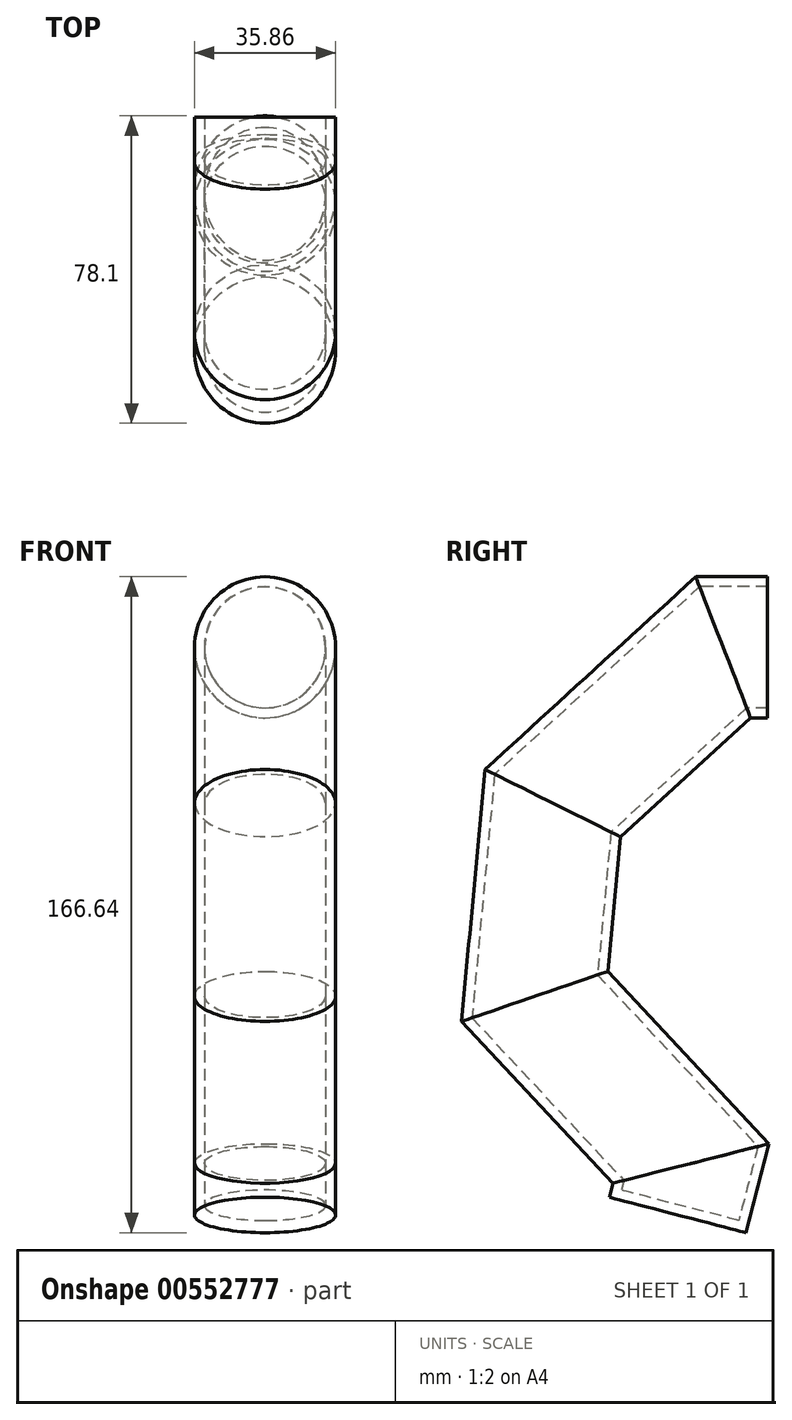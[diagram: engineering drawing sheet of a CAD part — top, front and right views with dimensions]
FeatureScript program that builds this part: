
annotation { "Feature Type Name" : "Feature", "Feature Type Description" : "" }
export const myFeature = defineFeature(function(context is Context, id is Id, definition is map)
    precondition{}
    {
        {
            var Q0;
            Q0=qCreatedBy(makeId("Front.planeOp"),FACE);
            var sketch = newSketch(context, id + "F0", { "sketchPlane" : qUnion([Q0])});
            skCircle(sketch, "E0", {"center": v(-8.39, 54.05) * mm, "radius": 17.93 * mm});
            skSolve(sketch);
        }
        {
            var Q0;
            Q0=qCreatedBy(makeId("Right.planeOp"),FACE);
            var sketch = newSketch(context, id + "F1", { "sketchPlane" : qUnion([Q0])});
            skLineSegment(sketch, "E1", {"start": v(0, 54.98) * mm, "end": v(-11.65, 54.98) * mm});
            skLineSegment(sketch, "E2", {"start": v(-11.65, 54.98) * mm, "end": v(-55.45, 14.9) * mm});
            skLineSegment(sketch, "E3", {"start": v(-55.45, 14.9) * mm, "end": v(-60.1, -34.95) * mm});
            skLineSegment(sketch, "E4", {"start": v(-60.1, -34.95) * mm, "end": v(-20.5, -77.35) * mm});
            skLineSegment(sketch, "E5", {"start": v(-20.5, -77.35) * mm, "end": v(-23.76, -89.93) * mm});
            skSolve(sketch);
        }
        {
            var Q0;
            Q0 = qSketchRegion(id + "F0", true);
            var Q1;
            Q1 = qConstructionFilter(qBodyType(qCreatedBy(id + "F1" ,EDGE), BodyType.WIRE), ConstructionObject.NO);
            sweep(context, id + "F2", {"profiles" : qUnion([Q0]), "path" : qUnion([Q1])});
        }
        {
            var Q0;
            Q0=makeQuery(id+"F2.opSweep","CAP_FACE",FACE,{"disambiguationData":[OSD([sQuery(id+"F0.wireOp",EDGE,"E0"),sQuery(id+"F1.wireOp",VERTEX,"E1.start")])],"isStart":true});
            shell(context, id + "F3", {"entities" : qUnion([Q0]), "thickness" : 2.54 * mm});
        }
    });
